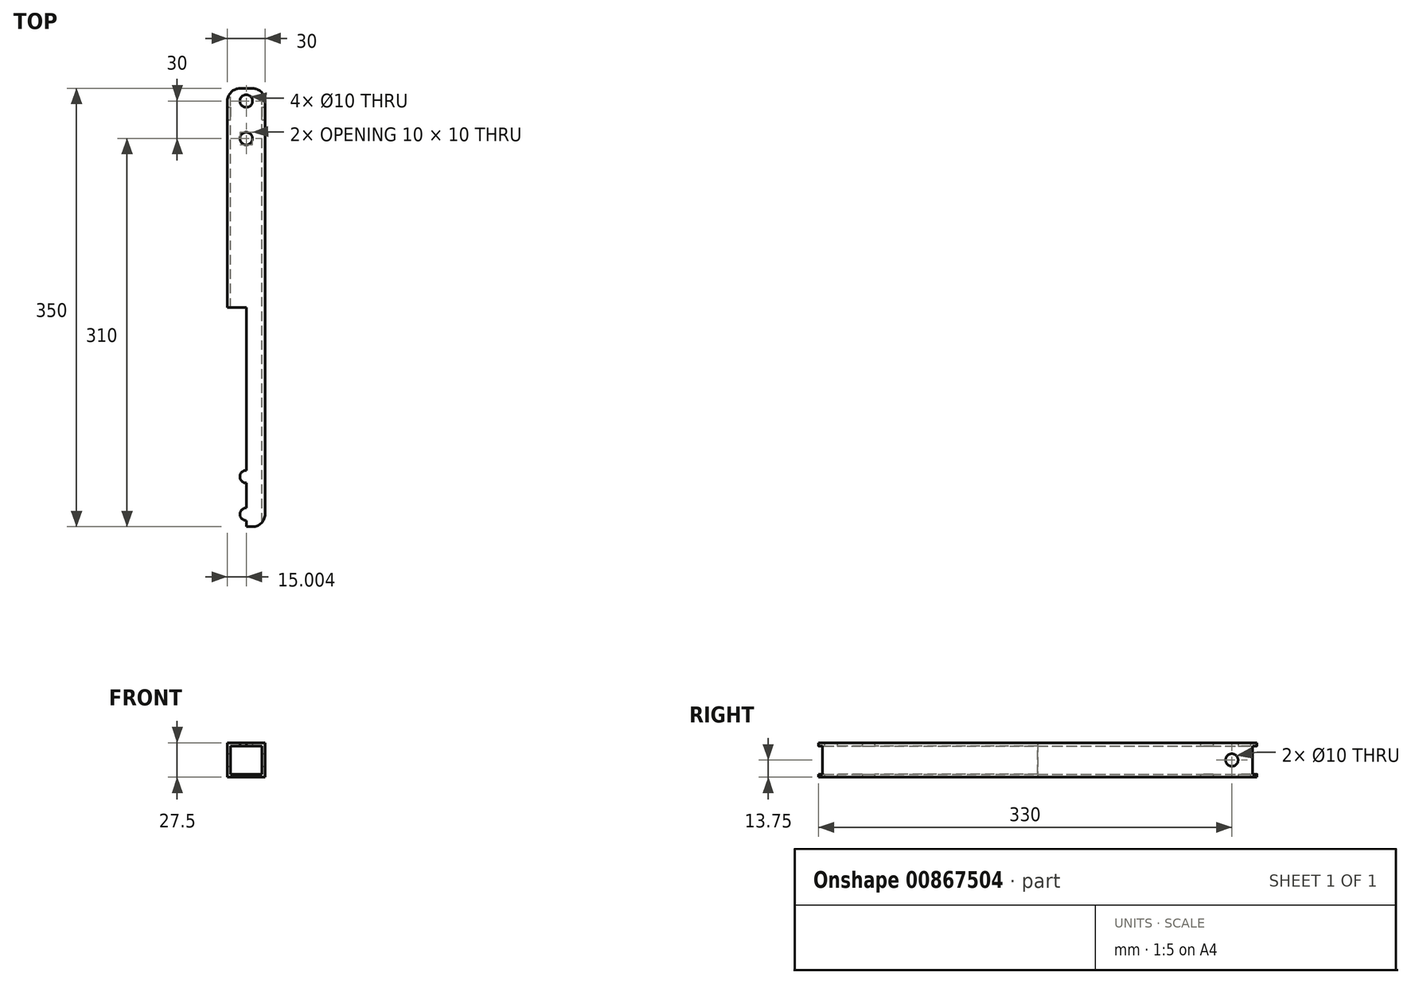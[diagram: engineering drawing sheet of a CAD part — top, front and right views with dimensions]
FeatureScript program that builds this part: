
annotation { "Feature Type Name" : "Feature", "Feature Type Description" : "" }
export const myFeature = defineFeature(function(context is Context, id is Id, definition is map)
    precondition{}
    {
        {
            var Q0;
            Q0=qCreatedBy(makeId("Front.planeOp"),FACE);
            var sketch = newSketch(context, id + "F0", { "sketchPlane" : qUnion([Q0])});
            skLineSegment(sketch, "E0.bottom", {"start": v(-74.99, 0) * mm, "end": v(-44.99, 0) * mm});
            skLineSegment(sketch, "E0.top", {"start": v(-74.99, 27.5) * mm, "end": v(-44.99, 27.5) * mm});
            skLineSegment(sketch, "E0.left", {"start": v(-74.99, 0) * mm, "end": v(-74.99, 27.5) * mm});
            skLineSegment(sketch, "E1.top", {"start": v(-47.49, 2.5) * mm, "end": v(-72.49, 2.5) * mm});
            skLineSegment(sketch, "E2.top", {"start": v(-47.49, 25) * mm, "end": v(-72.49, 25) * mm});
            skLineSegment(sketch, "E3", {"start": v(-72.49, 25) * mm, "end": v(-72.49, 2.5) * mm});
            skLineSegment(sketch, "E4.right", {"start": v(-47.49, 25) * mm, "end": v(-47.49, 2.5) * mm});
            skLineSegment(sketch, "E5", {"start": v(-44.99, 27.5) * mm, "end": v(-44.99, 0) * mm});
            skSolve(sketch);
        }
        {
            var Q0;
            Q0=makeQuery(id+"F0.imprint","IMPRINT",FACE,{"disambiguationData":[TD([[makeQuery(id+"F0.imprint","IMPRINT",EDGE,{"derivedFrom":sQuery(id+"F0.wireOp",EDGE,"E0.bottom")}),1.0]])]});
            extrude(context, id + "F1", {"entities" : qUnion([Q0]), "depth" : 350 * mm, "offsetDistance" : 25 * mm});
        }
        {
            var Q0;
            Q0=qCreatedBy(makeId("Top.planeOp"),FACE);
            var sketch = newSketch(context, id + "F2", { "sketchPlane" : qUnion([Q0])});
            skCircle(sketch, "E6", {"center": v(-59.99, -10) * mm, "radius": 5 * mm});
            skCircle(sketch, "E7", {"center": v(-59.99, -40) * mm, "radius": 5 * mm});
            skLineSegment(sketch, "E8.0", {"start": v(7.53, -175) * mm, "end": v(-74.99, -175) * mm, "construction": true});
            skCircle(sketch, "E9.MirrorC", {"center": v(-59.99, -310) * mm, "radius": 5 * mm});
            skCircle(sketch, "E10.MirrorC", {"center": v(-59.99, -340) * mm, "radius": 5 * mm});
            skLineSegment(sketch, "E11.bottom", {"start": v(-74.99, -175) * mm, "end": v(-59.99, -175) * mm});
            skLineSegment(sketch, "E11.top", {"start": v(-74.99, -350) * mm, "end": v(-59.99, -350) * mm});
            skLineSegment(sketch, "E11.left", {"start": v(-74.99, -175) * mm, "end": v(-74.99, -350) * mm});
            skLineSegment(sketch, "E11.right", {"start": v(-59.99, -175) * mm, "end": v(-59.99, -350) * mm});
            skLineSegment(sketch, "E12", {"start": v(-59.99, -340) * mm, "end": v(-59.99, -350) * mm});
            skLineSegment(sketch, "E13", {"start": v(-59.99, -175) * mm, "end": v(-59.99, 0) * mm});
            skSolve(sketch);
        }
        {
            var Q0;
            Q0=makeQuery(id+"F2.imprint","IMPRINT",FACE,{"disambiguationData":[TD([[makeQuery(id+"F2.imprint","IMPRINT",EDGE,{"derivedFrom":sQuery(id+"F2.wireOp",EDGE,"E10.MirrorC")}),-1.0]])]});
            var Q1;
            Q1=makeQuery(id+"F2.imprint","IMPRINT",FACE,{"disambiguationData":[TD([[makeQuery(id+"F2.imprint","IMPRINT",EDGE,{"derivedFrom":sQuery(id+"F2.wireOp",EDGE,"E7")}),1.0]])]});
            var Q2;
            Q2=makeQuery(id+"F2.imprint","IMPRINT",FACE,{"disambiguationData":[TD([[makeQuery(id+"F2.imprint","IMPRINT",EDGE,{"derivedFrom":sQuery(id+"F2.wireOp",EDGE,"E6")}),1.0]])]});
            var Q3;
            Q3=makeQuery(id+"F2.imprint","IMPRINT",FACE,{"disambiguationData":[TD([[makeQuery(id+"F2.imprint","IMPRINT",EDGE,{"derivedFrom":sQuery(id+"F2.wireOp",EDGE,"E9.MirrorC")}),-1.0]])]});
            extrude(context, id + "F3", {"entities" : qUnion([Q0, Q1, Q2, Q3]), "operationType" : NewBodyOperationType.REMOVE, "depth" : 53 * mm, "offsetDistance" : 25 * mm});
        }
        {
            var Q0;
            Q0=makeQuery(id+"F1.opExtrude","CAP_EDGE",EDGE,{"disambiguationData":[OSD([sQuery(id+"F0.wireOp",EDGE,"dc93dc5d-abfd-4881-bee3-2f176304b152.trimOffspring")])],"isStart":false});
            var Q1;
            Q1=makeQuery(id+"F1.opExtrude","CAP_EDGE",EDGE,{"disambiguationData":[OSD([sQuery(id+"F0.wireOp",EDGE,"E0.right")])],"isStart":false});
            var Q2;
            Q2=makeQuery(id+"F1.opExtrude","CAP_EDGE",EDGE,{"disambiguationData":[OSD([sQuery(id+"F0.wireOp",EDGE,"E0.right")])],"isStart":true});
            var Q3;
            Q3=makeQuery(id+"F1.opExtrude","CAP_EDGE",EDGE,{"disambiguationData":[OSD([sQuery(id+"F0.wireOp",EDGE,"dc93dc5d-abfd-4881-bee3-2f176304b152.trimOffspring")])],"isStart":true});
            var Q4;
            Q4=makeQuery(id+"F1.opExtrude","CAP_EDGE",EDGE,{"disambiguationData":[OSD([sQuery(id+"F0.wireOp",EDGE,"E0.left")])],"isStart":true});
            var Q5;
            Q5=makeQuery(id+"F1.opExtrude","CAP_EDGE",EDGE,{"disambiguationData":[OSD([sQuery(id+"F0.wireOp",EDGE,"E0.left")])],"isStart":false});
            var Q6;
            Q6=makeQuery(id+"F1.opExtrude","CAP_EDGE",EDGE,{"disambiguationData":[OSD([sQuery(id+"F0.wireOp",EDGE,"E5")])],"isStart":true});
            var Q7;
            Q7=makeQuery(id+"F1.opExtrude","CAP_EDGE",EDGE,{"disambiguationData":[OSD([sQuery(id+"F0.wireOp",EDGE,"E5")])],"isStart":false});
            fillet(context, id + "F4", {"entities" : qUnion([Q0, Q1, Q2, Q3, Q4, Q5, Q6, Q7]), "radius" : 10 * mm, "tangentPropagation" : true, "allowEdgeOverflow" : false});
        }
        {
            var Q0;
            Q0=makeQuery(id+"F1.opExtrude","SWEPT_FACE",FACE,{"disambiguationData":[OSD([sQuery(id+"F0.wireOp",EDGE,"E5")])]});
            var sketch = newSketch(context, id + "F5", { "sketchPlane" : qUnion([Q0])});
            skCircle(sketch, "E14", {"center": v(-20, 13.75) * mm, "radius": 5 * mm});
            skSolve(sketch);
        }
        {
            var Q0;
            Q0=makeQuery(id+"F5.imprint","IMPRINT",FACE,{"disambiguationData":[TD([[makeQuery(id+"F5.imprint","IMPRINT",EDGE,{"derivedFrom":sQuery(id+"F5.wireOp",EDGE,"E14")}),1.0]])]});
            extrude(context, id + "F6", {"entities" : qUnion([Q0]), "operationType" : NewBodyOperationType.REMOVE, "oppositeDirection" : true, "depth" : 37.8 * mm, "offsetDistance" : 25 * mm});
        }
    });
